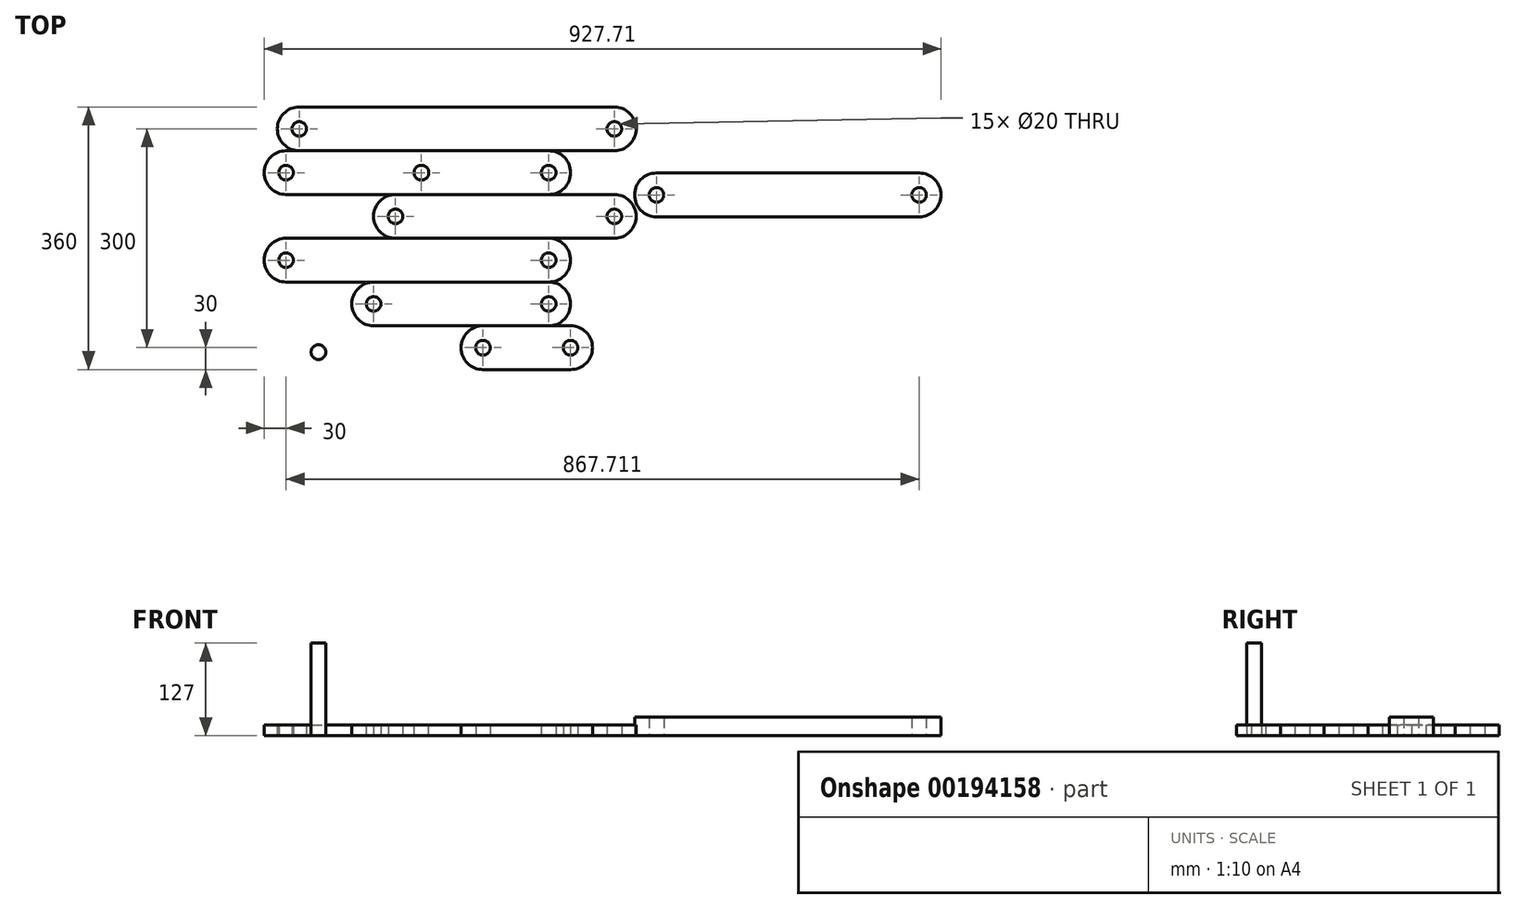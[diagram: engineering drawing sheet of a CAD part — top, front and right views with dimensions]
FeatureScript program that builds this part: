
annotation { "Feature Type Name" : "Feature", "Feature Type Description" : "" }
export const myFeature = defineFeature(function(context is Context, id is Id, definition is map)
    precondition{}
    {
        {
            var Q0;
            Q0=qCreatedBy(makeId("Top.planeOp"),FACE);
            var sketch = newSketch(context, id + "F0", { "sketchPlane" : qUnion([Q0])});
            skCircle(sketch, "E0", {"center": v(0, 0) * mm, "radius": 10 * mm});
            skArc(sketch, "E1", {"start": v(0, 30) * mm, "mid": v(-30, 0) * mm, "end": v(0, -30) * mm});
            skLineSegment(sketch, "E2", {"start": v(0, 30) * mm, "end": v(120, 30) * mm});
            skLineSegment(sketch, "E3", {"start": v(0, -30) * mm, "end": v(120, -30) * mm});
            skArc(sketch, "E4", {"start": v(120, -30) * mm, "mid": v(150, 0) * mm, "end": v(120, 30) * mm});
            skCircle(sketch, "E5", {"center": v(120, 0) * mm, "radius": 10 * mm});
            skSolve(sketch);
        }
        {
            var Q0;
            Q0=makeQuery(id+"F0.imprint","IMPRINT",FACE,{"disambiguationData":[TD([[makeQuery(id+"F0.imprint","IMPRINT",EDGE,{"derivedFrom":sQuery(id+"F0.wireOp",EDGE,"E0")}),-1.0]])]});
            extrude(context, id + "F1", {"entities" : qUnion([Q0]), "depth" : 15 * mm});
        }
        {
            var Q0;
            Q0=qCreatedBy(makeId("Top.planeOp"),FACE);
            var sketch = newSketch(context, id + "F2", { "sketchPlane" : qUnion([Q0])});
            skCircle(sketch, "E6", {"center": v(-150, 0) * mm, "radius": 10 * mm});
            skArc(sketch, "E7", {"start": v(-150, 30) * mm, "mid": v(-180, 0) * mm, "end": v(-150, -30) * mm});
            skLineSegment(sketch, "E8", {"start": v(-150, 30) * mm, "end": v(90, 30) * mm});
            skLineSegment(sketch, "E9", {"start": v(-150, -30) * mm, "end": v(90, -30) * mm});
            skArc(sketch, "E10", {"start": v(90, -30) * mm, "mid": v(120, 0) * mm, "end": v(90, 30) * mm});
            skCircle(sketch, "E11", {"center": v(90, 0) * mm, "radius": 10 * mm});
            skSolve(sketch);
        }
        {
            var Q0;
            Q0=makeQuery(id+"F2.imprint","IMPRINT",FACE,{"disambiguationData":[TD([[makeQuery(id+"F2.imprint","IMPRINT",EDGE,{"derivedFrom":sQuery(id+"F2.wireOp",EDGE,"E6")}),-1.0]])]});
            extrude(context, id + "F3", {"entities" : qUnion([Q0]), "depth" : 15 * mm});
        }
        {
            var Q0;
            Q0=makeQuery(id+"F3.opExtrude","SWEPT_BODY",BODY,{"disambiguationData":[OSD([sQuery(id+"F2.wireOp",EDGE,"E6"),sQuery(id+"F2.wireOp",EDGE,"E7"),sQuery(id+"F2.wireOp",EDGE,"E8"),sQuery(id+"F2.wireOp",EDGE,"E9"),sQuery(id+"F2.wireOp",EDGE,"E10"),sQuery(id+"F2.wireOp",EDGE,"E11")])]});
            transform(context, id + "F4", {"entities" : qUnion([Q0]), "transformType" : TransformType.TRANSLATION_3D, "dx" : 0 * mm, "dy" : 60 * mm, "dz" : 0 * mm, "makeCopy" : false});
        }
        {
            var Q0;
            Q0=qCreatedBy(makeId("Top.planeOp"),FACE);
            var sketch = newSketch(context, id + "F5", { "sketchPlane" : qUnion([Q0])});
            skCircle(sketch, "E12", {"center": v(-270, 0) * mm, "radius": 10 * mm});
            skArc(sketch, "E13", {"start": v(-270, 30) * mm, "mid": v(-300, 0) * mm, "end": v(-270, -30) * mm});
            skLineSegment(sketch, "E14", {"start": v(-270, 30) * mm, "end": v(90, 30) * mm});
            skLineSegment(sketch, "E15", {"start": v(-270, -30) * mm, "end": v(90, -30) * mm});
            skArc(sketch, "E16", {"start": v(90, -30) * mm, "mid": v(120, 0) * mm, "end": v(90, 30) * mm});
            skCircle(sketch, "E17", {"center": v(90, 0) * mm, "radius": 10 * mm});
            skSolve(sketch);
        }
        {
            var Q0;
            Q0=makeQuery(id+"F5.imprint","IMPRINT",FACE,{"disambiguationData":[TD([[makeQuery(id+"F5.imprint","IMPRINT",EDGE,{"derivedFrom":sQuery(id+"F5.wireOp",EDGE,"E12")}),-1.0]])]});
            extrude(context, id + "F6", {"entities" : qUnion([Q0]), "depth" : 15 * mm});
        }
        {
            var Q0;
            Q0=makeQuery(id+"F6.opExtrude","SWEPT_BODY",BODY,{"disambiguationData":[OSD([sQuery(id+"F5.wireOp",EDGE,"E12"),sQuery(id+"F5.wireOp",EDGE,"E13"),sQuery(id+"F5.wireOp",EDGE,"E14"),sQuery(id+"F5.wireOp",EDGE,"E15"),sQuery(id+"F5.wireOp",EDGE,"E16"),sQuery(id+"F5.wireOp",EDGE,"E17")])]});
            transform(context, id + "F7", {"entities" : qUnion([Q0]), "transformType" : TransformType.TRANSLATION_3D, "dx" : 0 * mm, "dy" : 120 * mm, "dz" : 0 * mm, "makeCopy" : false});
        }
        {
            var Q0;
            Q0=qCreatedBy(makeId("Top.planeOp"),FACE);
            var sketch = newSketch(context, id + "F8", { "sketchPlane" : qUnion([Q0])});
            skCircle(sketch, "E18", {"center": v(-120, 0) * mm, "radius": 10 * mm});
            skArc(sketch, "E19", {"start": v(-120, 30) * mm, "mid": v(-150, 0) * mm, "end": v(-120, -30) * mm});
            skLineSegment(sketch, "E20", {"start": v(-120, 30) * mm, "end": v(180, 30) * mm});
            skLineSegment(sketch, "E21", {"start": v(-120, -30) * mm, "end": v(180, -30) * mm});
            skArc(sketch, "E22", {"start": v(180, -30) * mm, "mid": v(210, 0) * mm, "end": v(180, 30) * mm});
            skCircle(sketch, "E23", {"center": v(180, 0) * mm, "radius": 10 * mm});
            skSolve(sketch);
        }
        {
            var Q0;
            Q0=makeQuery(id+"F8.imprint","IMPRINT",FACE,{"disambiguationData":[TD([[makeQuery(id+"F8.imprint","IMPRINT",EDGE,{"derivedFrom":sQuery(id+"F8.wireOp",EDGE,"E18")}),-1.0]])]});
            extrude(context, id + "F9", {"entities" : qUnion([Q0]), "depth" : 15 * mm});
        }
        {
            var Q0;
            Q0=makeQuery(id+"F9.opExtrude","SWEPT_BODY",BODY,{"disambiguationData":[OSD([sQuery(id+"F8.wireOp",EDGE,"E18"),sQuery(id+"F8.wireOp",EDGE,"E19"),sQuery(id+"F8.wireOp",EDGE,"E20"),sQuery(id+"F8.wireOp",EDGE,"E21"),sQuery(id+"F8.wireOp",EDGE,"E22"),sQuery(id+"F8.wireOp",EDGE,"E23")])]});
            transform(context, id + "F10", {"entities" : qUnion([Q0]), "transformType" : TransformType.TRANSLATION_3D, "dx" : 0 * mm, "dy" : 180 * mm, "dz" : 0 * mm, "makeCopy" : false});
        }
        {
            var Q0;
            Q0=qCreatedBy(makeId("Top.planeOp"),FACE);
            var sketch = newSketch(context, id + "F11", { "sketchPlane" : qUnion([Q0])});
            skCircle(sketch, "E24", {"center": v(-225.6, -5.99) * mm, "radius": 10.14 * mm});
            skSolve(sketch);
        }
        {
            var Q0;
            Q0=makeQuery(id+"F11.imprint","IMPRINT",FACE,{"disambiguationData":[TD([[makeQuery(id+"F11.imprint","IMPRINT",EDGE,{"derivedFrom":sQuery(id+"F11.wireOp",EDGE,"E24")}),1.0]])]});
            extrude(context, id + "F12", {"entities" : qUnion([Q0]), "depth" : 127 * mm, "offsetDistance" : 25.4 * mm});
        }
        {
            var Q0;
            Q0=makeQuery(id+"F6.opExtrude","SWEPT_BODY",BODY,{"disambiguationData":[OSD([sQuery(id+"F5.wireOp",EDGE,"E12"),sQuery(id+"F5.wireOp",EDGE,"E13"),sQuery(id+"F5.wireOp",EDGE,"E14"),sQuery(id+"F5.wireOp",EDGE,"E15"),sQuery(id+"F5.wireOp",EDGE,"E16"),sQuery(id+"F5.wireOp",EDGE,"E17")])]});
            transform(context, id + "F13", {"entities" : qUnion([Q0]), "transformType" : TransformType.TRANSLATION_3D, "dx" : 0 * mm, "dy" : 120 * mm, "dz" : 0 * mm, "makeCopy" : true});
        }
        {
            var Q0;
            Q0=makeQuery(id+"F13.opPattern","COPY",FACE,{"derivedFrom":makeQuery(id+"F6.opExtrude","CAP_FACE",FACE,{"disambiguationData":[OSD([sQuery(id+"F5.wireOp",EDGE,"E12"),sQuery(id+"F5.wireOp",EDGE,"E13"),sQuery(id+"F5.wireOp",EDGE,"E14"),sQuery(id+"F5.wireOp",EDGE,"E15"),sQuery(id+"F5.wireOp",EDGE,"E16"),sQuery(id+"F5.wireOp",EDGE,"E17")])],"isStart":false}),"instanceName":"1"});
            var sketch = newSketch(context, id + "F14", { "sketchPlane" : qUnion([Q0])});
            skCircle(sketch, "E25", {"center": v(-84.43, 240) * mm, "radius": 10 * mm});
            skSolve(sketch);
        }
        {
            var Q0;
            Q0=makeQuery(id+"F14.imprint","IMPRINT",FACE,{"disambiguationData":[TD([[makeQuery(id+"F14.imprint","IMPRINT",EDGE,{"derivedFrom":sQuery(id+"F14.wireOp",EDGE,"E25")}),1.0]])]});
            extrude(context, id + "F15", {"entities" : qUnion([Q0]), "operationType" : NewBodyOperationType.REMOVE, "endBound" : BoundingType.THROUGH_ALL, "oppositeDirection" : true, "depth" : 25 * mm});
        }
        {
            var Q0;
            Q0=qCreatedBy(makeId("Top.planeOp"),FACE);
            var sketch = newSketch(context, id + "F16", { "sketchPlane" : qUnion([Q0])});
            skCircle(sketch, "E26", {"center": v(-252, 0) * mm, "radius": 10 * mm});
            skArc(sketch, "E27", {"start": v(-252, 30) * mm, "mid": v(-282, 0) * mm, "end": v(-252, -30) * mm});
            skLineSegment(sketch, "E28", {"start": v(-252, 30) * mm, "end": v(180, 30) * mm});
            skLineSegment(sketch, "E29", {"start": v(-252, -30) * mm, "end": v(180, -30) * mm});
            skArc(sketch, "E30", {"start": v(180, -30) * mm, "mid": v(210, 0) * mm, "end": v(180, 30) * mm});
            skCircle(sketch, "E31", {"center": v(180, 0) * mm, "radius": 10 * mm});
            skSolve(sketch);
        }
        {
            var Q0;
            Q0 = qSketchRegion(id + "F16", true);
            extrude(context, id + "F17", {"entities" : qUnion([Q0]), "depth" : 15 * mm});
        }
        {
            var Q0;
            Q0=makeQuery(id+"F17.opExtrude","SWEPT_BODY",BODY,{"disambiguationData":[OSD([sQuery(id+"F16.wireOp",EDGE,"E26"),sQuery(id+"F16.wireOp",EDGE,"E27"),sQuery(id+"F16.wireOp",EDGE,"E28"),sQuery(id+"F16.wireOp",EDGE,"E29"),sQuery(id+"F16.wireOp",EDGE,"E30"),sQuery(id+"F16.wireOp",EDGE,"E31")])]});
            transform(context, id + "F18", {"entities" : qUnion([Q0]), "transformType" : TransformType.TRANSLATION_3D, "dx" : 0 * mm, "dy" : 300 * mm, "dz" : 0 * mm, "makeCopy" : false});
        }
        {
            var Q0;
            Q0=qCreatedBy(makeId("Top.planeOp"),FACE);
            var sketch = newSketch(context, id + "F19", { "sketchPlane" : qUnion([Q0])});
            skCircle(sketch, "E32", {"center": v(237.71, 209.5) * mm, "radius": 10 * mm});
            skArc(sketch, "E33", {"start": v(237.71, 239.5) * mm, "mid": v(207.71, 209.5) * mm, "end": v(237.71, 179.5) * mm});
            skLineSegment(sketch, "E34", {"start": v(237.71, 239.5) * mm, "end": v(597.71, 239.5) * mm});
            skLineSegment(sketch, "E35", {"start": v(237.71, 179.5) * mm, "end": v(597.71, 179.5) * mm});
            skArc(sketch, "E36", {"start": v(597.71, 179.5) * mm, "mid": v(627.71, 209.5) * mm, "end": v(597.71, 239.5) * mm});
            skCircle(sketch, "E37", {"center": v(597.71, 209.5) * mm, "radius": 10 * mm});
            skSolve(sketch);
        }
        {
            var Q0;
            Q0 = qSketchRegion(id + "F19", true);
            extrude(context, id + "F20", {"entities" : qUnion([Q0]), "depth" : 25.4 * mm, "offsetDistance" : 25.4 * mm});
        }
    });
